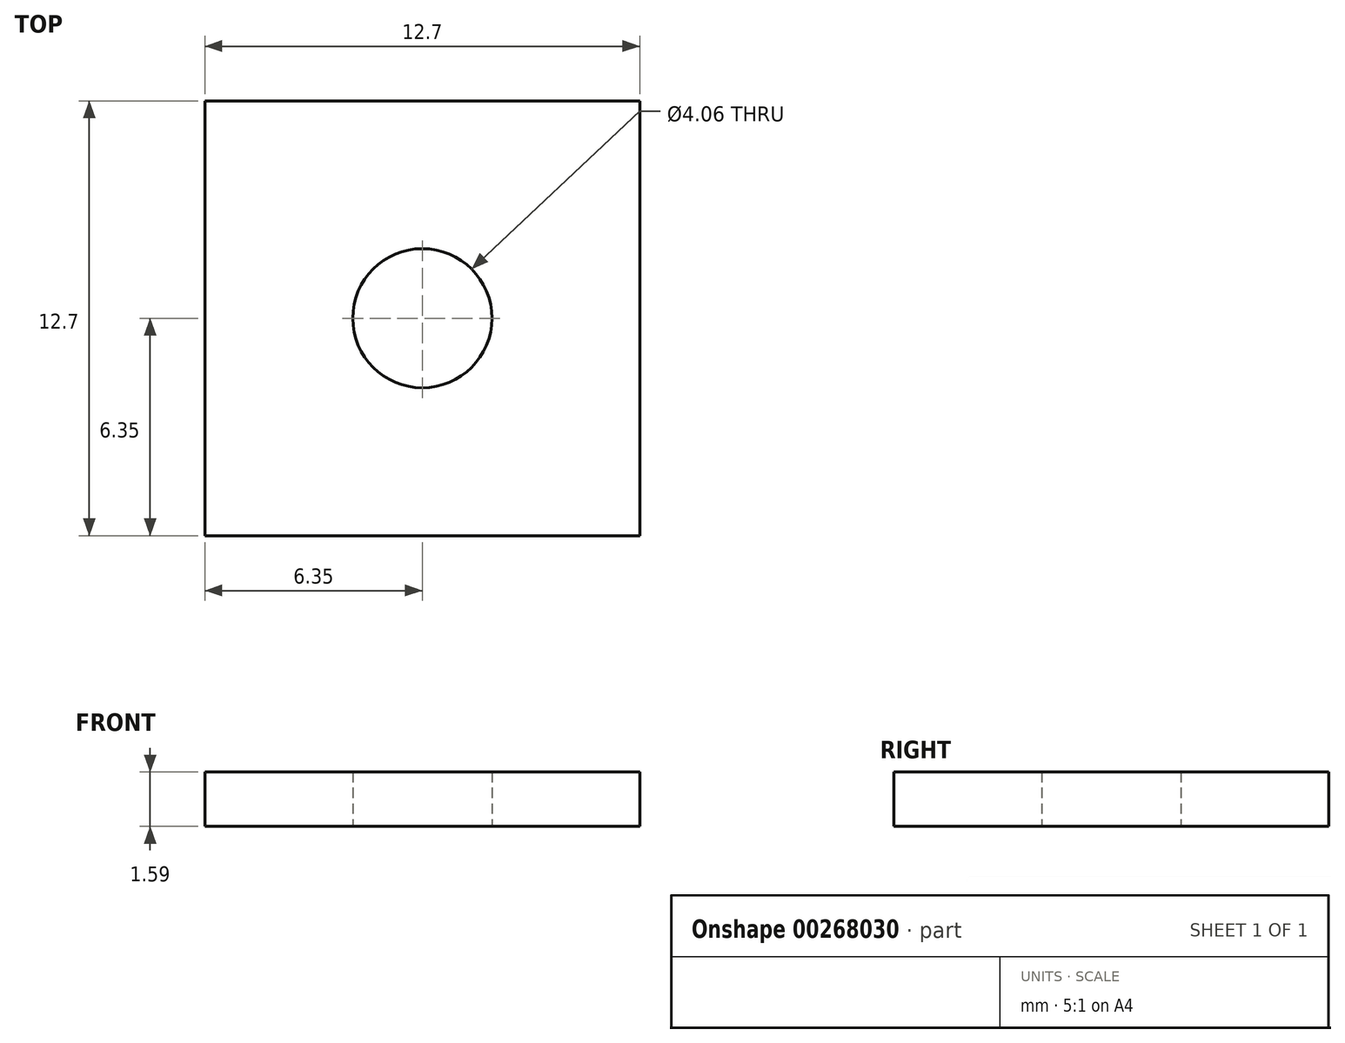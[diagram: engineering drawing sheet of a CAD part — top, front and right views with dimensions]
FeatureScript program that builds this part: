
annotation { "Feature Type Name" : "Feature", "Feature Type Description" : "" }
export const myFeature = defineFeature(function(context is Context, id is Id, definition is map)
    precondition{}
    {
        {
            var Q0;
            Q0=qCreatedBy(makeId("Top.planeOp"),FACE);
            var sketch = newSketch(context, id + "F0", { "sketchPlane" : qUnion([Q0])});
            skLineSegment(sketch, "E0.bottom", {"start": v(6.35, -6.35) * mm, "end": v(-6.35, -6.35) * mm});
            skLineSegment(sketch, "E0.top", {"start": v(6.35, 6.35) * mm, "end": v(-6.35, 6.35) * mm});
            skLineSegment(sketch, "E0.left", {"start": v(6.35, -6.35) * mm, "end": v(6.35, 6.35) * mm});
            skLineSegment(sketch, "E0.right", {"start": v(-6.35, -6.35) * mm, "end": v(-6.35, 6.35) * mm});
            skPoint(sketch, "E0.middle", {"position": v(0, 0) * mm});
            skCircle(sketch, "E1", {"center": v(0, 0) * mm, "radius": 2.03 * mm});
            skSolve(sketch);
        }
        {
            var Q0;
            Q0=makeQuery(id+"F0.imprint","IMPRINT",FACE,{"disambiguationData":[TD([[makeQuery(id+"F0.imprint","IMPRINT",EDGE,{"derivedFrom":sQuery(id+"F0.wireOp",EDGE,"E0.bottom")}),-1.0]])]});
            extrude(context, id + "F1", {"entities" : qUnion([Q0]), "depth" : 1.59 * mm, "offsetDistance" : 25.4 * mm});
        }
    });
